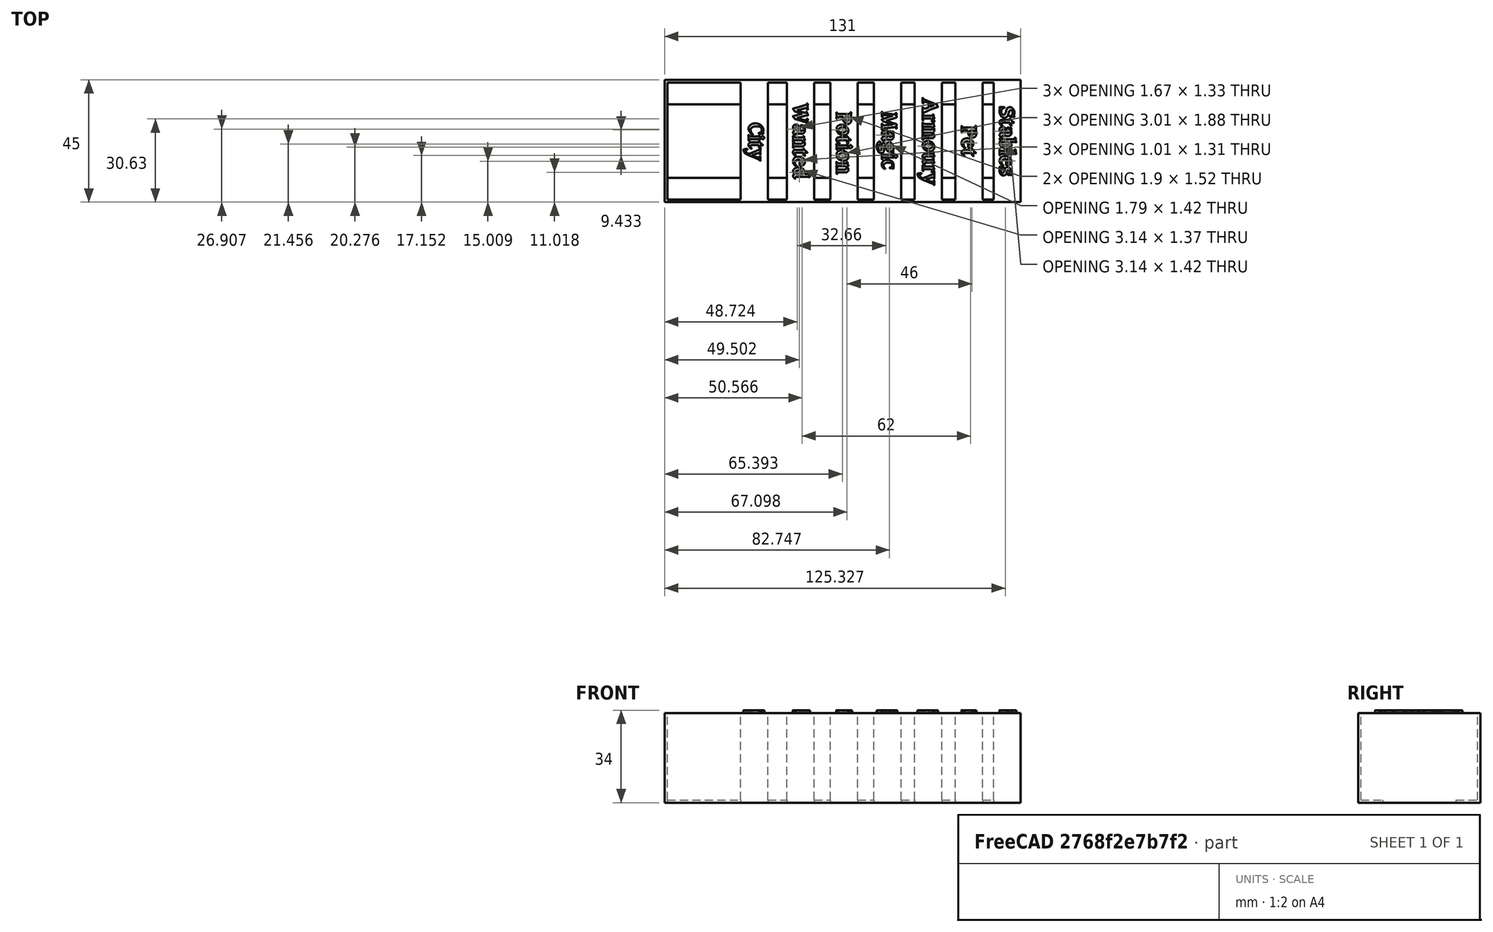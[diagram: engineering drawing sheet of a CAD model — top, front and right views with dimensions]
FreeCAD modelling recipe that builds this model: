
FCSTD DOCUMENT  (FreeCAD 0.18R4 (GitTag))
Label: city
License: All rights reserved
LicenseURL: http://en.wikipedia.org/wiki/All_rights_reserved
objects: Part::Box×12, Part::Part2DObjectPython×7, Part::Extrusion×7, Part::MultiFuse×3, Part::Cut×2
note: 31 computed .brp shape members not serialized (recipe doc carries the construction recipe); baked Part::Feature solids carry a one-line shape summary decoded from their .brp

FEATURE [Part::Box] Box  label="Cube"
  AttacherType = Attacher::AttachEngine3D
  Height = 33
  Length = 202
  Placement = pos=(0,-1,0) rot=(0,0,1;0rad)
  Width = 45
FEATURE [Part::Box] Box001  label="Cube001"
  AttacherType = Attacher::AttachEngine3D
  Height = 33
  Length = 200
  Placement = pos=(1,0,0) rot=(0,0,1;0rad)
  Width = 43
FEATURE [Part::Cut] Cut
  Base = -> Box
  Tool = -> Box001
FEATURE [Part::Box] Box002  label="Cube002"
  AttacherType = Attacher::AttachEngine3D
  Height = 1
  Length = 202
  Width = 8
FEATURE [Part::Box] Box003  label="Cube003"
  AttacherType = Attacher::AttachEngine3D
  Height = 1
  Length = 202
  Placement = pos=(0,35,0) rot=(0,0,1;0rad)
  Width = 8
FEATURE [Part::MultiFuse] Fusion
  Shapes = -> [Cut,Box002,Box003]
FEATURE [Part::Box] Box004  label="Cube004"
  AttacherType = Attacher::AttachEngine3D
  Height = 33
  Length = 10
  Placement = pos=(28,0,0) rot=(0,0,1;0rad)
  Width = 43
FEATURE [Part::Box] Box005  label="Cube005"
  AttacherType = Attacher::AttachEngine3D
  Height = 33
  Length = 10
  Placement = pos=(45,0,0) rot=(0,0,1;0rad)
  Width = 43
FEATURE [Part::Box] Box006  label="Cube006"
  AttacherType = Attacher::AttachEngine3D
  Height = 33
  Length = 10
  Placement = pos=(61,0,0) rot=(0,0,1;0rad)
  Width = 43
FEATURE [Part::Box] Box007  label="Cube007"
  AttacherType = Attacher::AttachEngine3D
  Height = 33
  Length = 10
  Placement = pos=(77,0,0) rot=(0,0,1;0rad)
  Width = 43
FEATURE [Part::Box] Box008  label="Cube008"
  AttacherType = Attacher::AttachEngine3D
  Height = 33
  Length = 10
  Placement = pos=(92,0,0) rot=(0,0,1;0rad)
  Width = 43
FEATURE [Part::Box] Box009  label="Cube009"
  AttacherType = Attacher::AttachEngine3D
  Height = 33
  Length = 10
  Placement = pos=(107,0,0) rot=(0,0,1;0rad)
  Width = 43
FEATURE [Part::Box] Box010  label="Cube010"
  AttacherType = Attacher::AttachEngine3D
  Height = 33
  Length = 10
  Placement = pos=(121,0,0) rot=(0,0,1;0rad)
  Width = 43
FEATURE [Part::Box] Box011  label="Cube011"
  AttacherType = Attacher::AttachEngine3D
  Height = 33
  Length = 72
  Placement = pos=(131,-2,0) rot=(0,0,1;0rad)
  Width = 47
FEATURE [Part::MultiFuse] Fusion001
  Shapes = -> [Fusion,Box005,Box006,Box009,Box008,Box007,Box010,Box004]
FEATURE [Part::Cut] Cut001
  Base = -> Fusion001
  Tool = -> Box011
FEATURE [Part::Part2DObjectPython] ShapeString  # Draft 2D object (typed FeaturePython)
  FontFile = <userpath>/Downloads/talisman/Caxton Bold.otf
  Placement = pos=(40,28.31,33) rot=(0,0,-1;1.5708rad)
  Size = 3
  String = City
  Tracking = 0
FEATURE [Part::Part2DObjectPython] ShapeString001  # Draft 2D object (typed FeaturePython)
  FontFile = <userpath>/Downloads/talisman/Caxton Bold.otf
  Placement = pos=(57.34,35.31,33) rot=(0,0,-1;1.5708rad)
  Size = 3
  String = Wanted
  Tracking = 0
FEATURE [Part::Part2DObjectPython] ShapeString002  # Draft 2D object (typed FeaturePython)
  FontFile = <userpath>/Downloads/talisman/Caxton Bold.otf
  Placement = pos=(73.34,32.31,33) rot=(0,0,-1;1.5708rad)
  Size = 3
  String = Potion
  Tracking = 0
FEATURE [Part::Part2DObjectPython] ShapeString003  # Draft 2D object (typed FeaturePython)
  FontFile = <userpath>/Downloads/talisman/Caxton Bold.otf
  Placement = pos=(90,32.31,33) rot=(0,0,-1;1.5708rad)
  Size = 3
  String = Magic
  Tracking = 0
FEATURE [Part::Part2DObjectPython] ShapeString004  # Draft 2D object (typed FeaturePython)
  FontFile = <userpath>/Downloads/talisman/Caxton Bold.otf
  Placement = pos=(105,37.31,33) rot=(0,0,-1;1.5708rad)
  Size = 3
  String = Armoury
  Tracking = 0
FEATURE [Part::Part2DObjectPython] ShapeString005  # Draft 2D object (typed FeaturePython)
  FontFile = <userpath>/Downloads/talisman/Caxton Bold.otf
  Placement = pos=(119.34,27.31,33) rot=(0,0,-1;1.5708rad)
  Size = 3
  String = Pet
  Tracking = 0
FEATURE [Part::Part2DObjectPython] ShapeString006  # Draft 2D object (typed FeaturePython)
  FontFile = <userpath>/Downloads/talisman/Caxton Bold.otf
  Placement = pos=(133.34,34.31,33) rot=(0,0,-1;1.5708rad)
  Size = 3
  String = Stables
  Tracking = 0
FEATURE [Part::Extrusion] Extrude
  Base = -> ShapeString
  Dir = (0,0,1)
  DirMode = 2
  FaceMakerClass = Part::FaceMakerBullseye
  LengthFwd = 1
  LengthRev = 0
  Placement = pos=(-9,0,0) rot=(0,0,1;0rad)
  Solid = false
  Symmetric = false
FEATURE [Part::Extrusion] Extrude001
  Base = -> ShapeString001
  Dir = (0,0,1)
  DirMode = 2
  FaceMakerClass = Part::FaceMakerBullseye
  LengthFwd = 1
  LengthRev = 0
  Placement = pos=(-10,0,0) rot=(0,0,1;0rad)
  Solid = false
  Symmetric = false
FEATURE [Part::Extrusion] Extrude002
  Base = -> ShapeString002
  Dir = (0,0,1)
  DirMode = 2
  FaceMakerClass = Part::FaceMakerBullseye
  LengthFwd = 1
  LengthRev = 0
  Placement = pos=(-10,0,0) rot=(0,0,1;0rad)
  Solid = false
  Symmetric = false
FEATURE [Part::Extrusion] Extrude003
  Base = -> ShapeString003
  Dir = (0,0,1)
  DirMode = 2
  FaceMakerClass = Part::FaceMakerBullseye
  LengthFwd = 1
  LengthRev = 0
  Placement = pos=(-10,0,0) rot=(0,0,1;0rad)
  Solid = false
  Symmetric = false
FEATURE [Part::Extrusion] Extrude004
  Base = -> ShapeString004
  Dir = (0,0,1)
  DirMode = 2
  FaceMakerClass = Part::FaceMakerBullseye
  LengthFwd = 1
  LengthRev = 0
  Placement = pos=(-10,0,0) rot=(0,0,1;0rad)
  Solid = false
  Symmetric = false
FEATURE [Part::Extrusion] Extrude005
  Base = -> ShapeString005
  Dir = (0,0,1)
  DirMode = 2
  FaceMakerClass = Part::FaceMakerBullseye
  LengthFwd = 1
  LengthRev = 0
  Placement = pos=(-10,0,0) rot=(0,0,1;0rad)
  Solid = false
  Symmetric = false
FEATURE [Part::Extrusion] Extrude006
  Base = -> ShapeString006
  Dir = (0,0,1)
  DirMode = 2
  FaceMakerClass = Part::FaceMakerBullseye
  LengthFwd = 1
  LengthRev = 0
  Placement = pos=(-10,0,0) rot=(0,0,1;0rad)
  Solid = false
  Symmetric = false
FEATURE [Part::MultiFuse] Fusion003
  Shapes = -> [Extrude003,Extrude002,Extrude004,Extrude,Extrude005,Extrude001,Extrude006]
